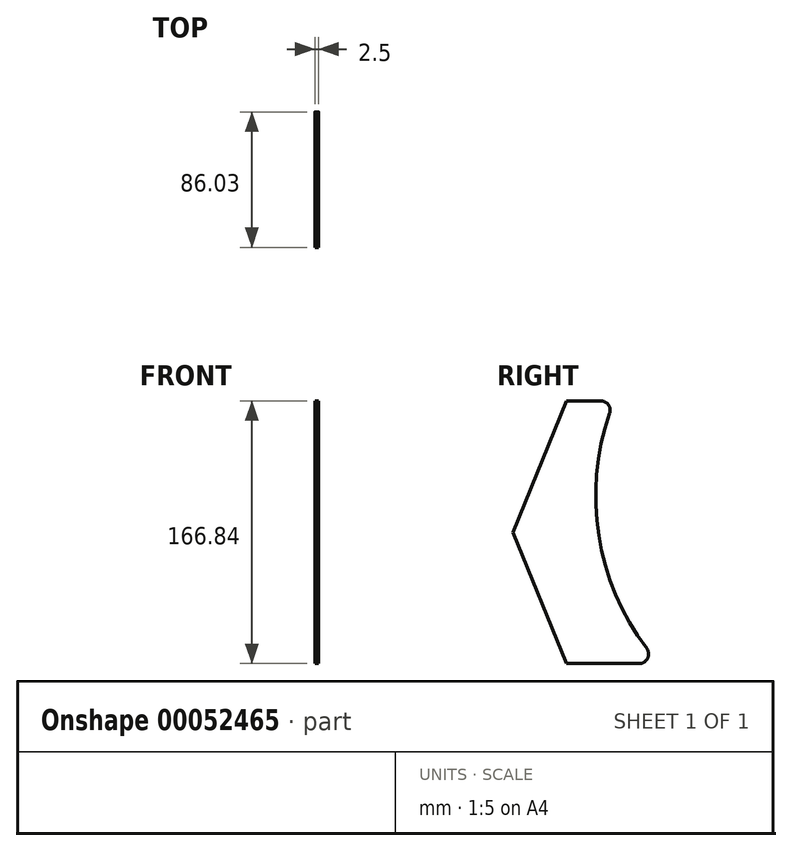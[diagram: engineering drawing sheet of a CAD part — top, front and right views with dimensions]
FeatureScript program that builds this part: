
annotation { "Feature Type Name" : "Feature", "Feature Type Description" : "" }
export const myFeature = defineFeature(function(context is Context, id is Id, definition is map)
    precondition{}
    {
        {
            var Q0;
            Q0=qCreatedBy(makeId("Right.planeOp"),FACE);
            var sketch = newSketch(context, id + "F0", { "sketchPlane" : qUnion([Q0])});
            skLineSegment(sketch, "E0", {"start": v(0, 174.52) * mm, "end": v(0, -183.34) * mm, "construction": true});
            skLineSegment(sketch, "E1", {"start": v(185.16, 0) * mm, "end": v(-253.1, 0) * mm, "construction": true});
            skLineSegment(sketch, "E2", {"start": v(-8.68, 83.42) * mm, "end": v(-30.6, 83.42) * mm});
            skLineSegment(sketch, "E3", {"start": v(-30.6, 83.42) * mm, "end": v(-64.3, 0) * mm});
            skLineSegment(sketch, "E4", {"start": v(-64.3, 0) * mm, "end": v(-30.6, -83.42) * mm});
            skLineSegment(sketch, "E5", {"start": v(-30.6, -83.42) * mm, "end": v(15.73, -83.42) * mm});
            skArc(sketch, "E6", {"start": v(-3.02, 75.44) * mm, "mid": v(-9.97, -2.13) * mm, "end": v(20.51, -73.8) * mm});
            skPoint(sketch, "E7.visualSharp", {"position": v(0, 83.42) * mm});
            skArc(sketch, "E7.filletArc", {"start": v(-3.02, 75.44) * mm, "mid": v(-3.8, 80.9) * mm, "end": v(-8.68, 83.42) * mm});
            skPoint(sketch, "E8.visualSharp", {"position": v(28.4, -83.42) * mm});
            skArc(sketch, "E8.filletArc", {"start": v(15.73, -83.42) * mm, "mid": v(21.1, -80.1) * mm, "end": v(20.51, -73.8) * mm});
            skLineSegment(sketch, "E9", {"start": v(68.5, -83.42) * mm, "end": v(-156.84, -83.42) * mm, "construction": true});
            skPoint(sketch, "E9.endSnap0", {"position": v(-7.44, -83.42) * mm});
            skLineSegment(sketch, "E10", {"start": v(-30.6, -141.65) * mm, "end": v(-30.6, 147) * mm, "construction": true});
            skLineSegment(sketch, "E11", {"start": v(-64.3, 145.58) * mm, "end": v(-64.3, -148.5) * mm, "construction": true});
            skLineSegment(sketch, "E12", {"start": v(-120.6, 80.9) * mm, "end": v(-120.6, 83.42) * mm, "construction": true});
            skPoint(sketch, "E12.startSnap0", {"position": v(-3.8, 80.9) * mm});
            skLineSegment(sketch, "E13", {"start": v(-120.6, 83.42) * mm, "end": v(78.66, 83.42) * mm, "construction": true});
            skSolve(sketch);
        }
        {
            var Q0;
            Q0 = qSketchRegion(id + "F0", true);
            extrude(context, id + "F1", {"entities" : qUnion([Q0]), "depth" : 2.5 * mm});
        }
    });
